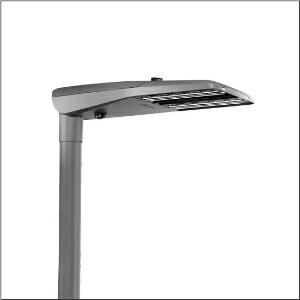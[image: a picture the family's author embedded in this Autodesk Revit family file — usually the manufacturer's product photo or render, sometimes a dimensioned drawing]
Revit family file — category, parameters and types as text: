
# Revit family: streetlight_sl_11_iq_midi___st1_2a_5xc3a41y08me_bddd
name_source: partatom
category: Lighting Fixtures
units: mm (PartAtom-declared; Revit-internal decimal feet)

## family parameters
Cut with Voids When Loaded = No
Host = Face
Light Source = No
Part Type = Normal
Room Calculation Point = No
Round Connector Dimension = Use Diameter
Shared = No

## types (1)
- --- (1 x LED, 18900 lm, 122.6 W, 4000K)
    Apparent Load = 123 VA
    CIE Flux Codes = 32 70 96 100 100
    Color Rendering = 70
    Color Temperature = 4000K
    Default Elevation = 1800 mm
    Description = Streetlight SL 11 iQ midi, mast luminaire, primary light control with 3 zone facetted reflector, of plastic, silver coated, highly specular, primary optical cover: cover, of PMMA, transparent, light distribution: ST1.2a, light emission: direct distribution, primary light characteristic: asymmetric, installation type: post-top, side-entry, lamps: LED, High Power LED, rated values: 18.900lm | 122,6W | 154,2lm/W (begin service life); end service life: 18.900lm | 130,2W; at 50% lumin. flux: 9.450lm | 56,3W | 167,9lm/W, colour temperature: 4000K, colour rendering: CRI > 70, light colour: 740, light setting 1 begin service life: 100% | 18.900lm | 122,6W | 154,2lm/W | 4.000K, light setting 1 end service life: 130,2W, further light settings possible, control: pre-setting: logarithmic dimming characteristic, Street-Remote, Auto-Match, Temp-Guard, Lumen-Switch, Night-Set, Smart-Wire, Light-Fading, Desk-Remote (wireless, voltage-free reading and setting of iQ features in the workshop via application-optimized NFC function/RFID function), optimised constant luminous flux control (CLO 2.0), with cable H07RN-F 5x 1.5mm², mains connection: 230..240V, AC, 50/60Hz, connection cable pre-assembled, cable length: 12,5m, luminaire housing, of diecast aluminium, powder-coated, Siteco® metallic grey (DB 702S), please order mast flange separately, inclination adjustable without tools: 0°, 5°, 10°, 15° (post-top) | 0°, -5°, -10°, -15° (side-entry), sealing non-destructively replaceable, multi-level sealing system, length: 780mm, width: 376mm, height: 118mm, mast flange for spigot size: 42mm (side-entry): 5XC10008XM4, 60/48mm (side-entry/post-top): 5XC10108XM2, 76/60mm (side-entry/post-top): 5XC10108XM1, equipment: Power, Smart Interface below and above, protection rating (complete): IP66, insulation class (complete): insulation class II (safety insulation), certification: CE, ENEC, ENEC+, VDE, UKCA, impact resistance: IK10, permissible operating ambient temperature for outdoor applications: -25..+50°C, standard-compliant lighting for roads and squares, Environmental Product Declaration (EPD) tested and certified by an independent institute, packaging unit: 1 piece

Light Distribution: ST1.2a
    Height = 118 mm
    Lamp = 1 x LED
    Lamp Light Flux = 18900 lm
    Lamp Power = 122.6 W
    Lamp count = 1
    Length = 780 mm
    Luminous efficacy = 154 lm/W
    Manufacturer = Siteco
    ModVariant = No
    Model = 5XC3A41Y08ME
    Number of Poles = 1
    OnlyDefault = Yes
    Power Factor = 1
    Product Name = Streetlight SL 11 iQ midi | ST1.2a
    Product group = mast luminaire | pylon top
    ProductGroupID = 6100
    Protection Class = Protection class II
    Protection Degree = IP 66
    RLX_Detail_Level = 1
    RLX_Emergency_Light_Flux = 0 lm
    RLX_Emergency_Type = 0
    RLX_Emergency_Type_DB = No
    RlxData = <blob elided: 69901 chars, md5=2eb5a8ea>
    Socket = socket
    Standby Power = 0 W
    System Light Flux = 18900 lm
    System Power = 123 W
    Type Comments = factory setting: luminous flux: 100 % | dim-lin: 254 | 552 mA
    Type Image = l_1004429.jpg
    URL = http://relux.com
    VarID = @adj_136471
    Voltage = 0 V
    Weight = 0.00 kg
    Width = 376 mm

## geometry (parser evidence)
native form markers: Blend x4, Sweep x10
no freeform markers — native parametric forms only
